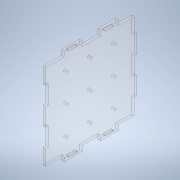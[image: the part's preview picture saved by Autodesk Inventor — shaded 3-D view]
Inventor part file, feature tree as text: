
AUTODESK INVENTOR PART (.ipt)
format: ipt  version: 2020 (Build 240168000, 168)  size: 186,880 bytes
history: native  units: mm
features: sketch x10, hole x9, extrude x1
ambient origin geometry x8: Origin, YZ Plane, XZ Plane, XY Plane, X Axis, Y Axis, Z Axis, Center Point
bodies: Solid1 (feature_tree)
feature tree (20):
  extrude  "Extrusion1"  Depth=3.0mm
  hole  "Hole2"  [1 undecoded]
  hole  "Hole3"  [1 undecoded]
  hole  "Hole4"  [1 undecoded]
  hole  "Hole5"  [1 undecoded]
  hole  "Hole6"  [1 undecoded]
  hole  "Hole7"  [1 undecoded]
  hole  "Hole8"  [1 undecoded]
  hole  "Hole9"  [1 undecoded]
  hole  "Hole10"  [1 undecoded]
  sketch  "Sketch1"  dims[d4=3.0mm d5=0.0mm d22=3.0mm]
  sketch  "Sketch3"  dims[d23=3.0mm d24=6.0mm d25=4.0mm d26=2.0mm d27=90.0deg d28=8.0mm d29=20.594885mm d30=3.0mm]
  sketch  "Sketch4"  dims[d31=3.0mm d32=6.0mm d33=4.0mm d34=2.0mm d35=90.0deg d36=8.0mm d37=20.594885mm d38=3.0mm]
  sketch  "Sketch5"  dims[d39=3.0mm d40=6.0mm d41=4.0mm d42=2.0mm d43=90.0deg d44=8.0mm d45=20.594885mm d46=3.0mm]
  sketch  "Sketch6"  dims[d47=3.0mm d48=6.0mm d49=4.0mm d50=2.0mm d51=90.0deg d52=8.0mm d53=20.594885mm d54=3.0mm]
  sketch  "Sketch7"  dims[d55=3.0mm d56=6.0mm d57=4.0mm d58=2.0mm d59=90.0deg d60=8.0mm d61=20.594885mm d62=3.0mm]
  sketch  "Sketch8"  dims[d63=3.0mm d64=6.0mm d65=4.0mm d66=2.0mm d67=90.0deg d68=8.0mm d69=20.594885mm d70=3.0mm]
  sketch  "Sketch9"  dims[d71=3.0mm d72=6.0mm d73=4.0mm d74=2.0mm d75=90.0deg d76=8.0mm d77=20.594885mm d78=3.0mm]
  sketch  "Sketch10"  dims[d79=3.0mm d80=6.0mm d81=4.0mm d82=2.0mm d83=90.0deg d84=8.0mm d85=20.594885mm d86=3.0mm]
  sketch  "Sketch11"  dims[d87=3.0mm d88=6.0mm d89=4.0mm d90=2.0mm d91=90.0deg d92=8.0mm d93=20.594885mm d94=1.0mm d95=10.0mm d96=1.0mm d97=10.0mm d98=10.0mm d99=1.0mm d100=10.0mm]
note: 9 required parameter values undecoded (feature->parameter linkage not recoverable at this tier; creation-order binding heuristic only, values carry confidence <= 0.55)
